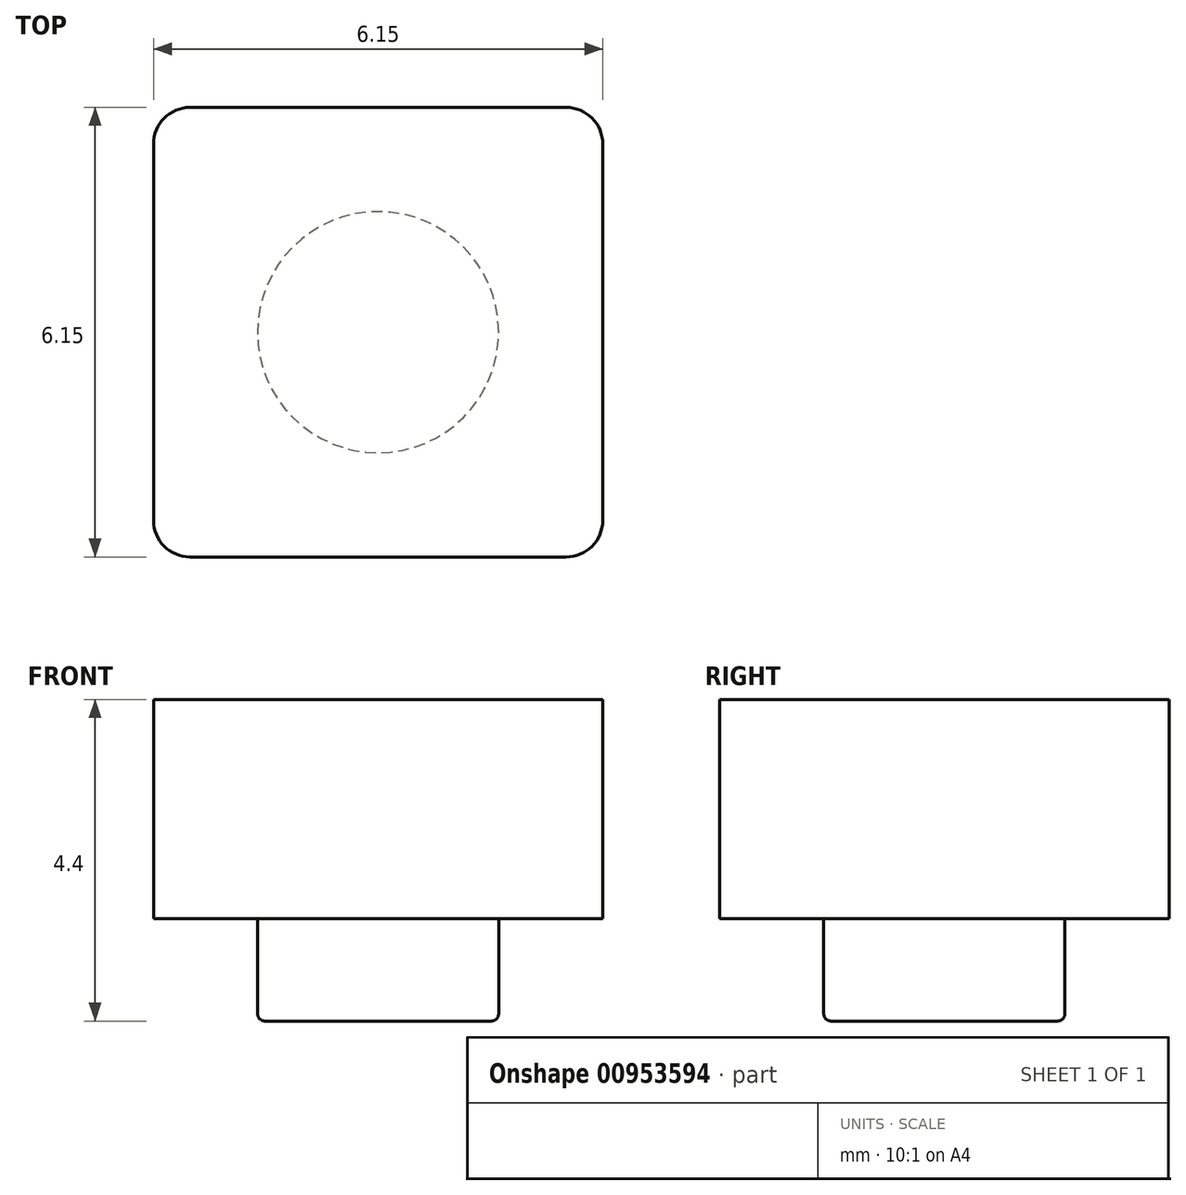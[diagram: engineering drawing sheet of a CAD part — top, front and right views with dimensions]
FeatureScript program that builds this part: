
annotation { "Feature Type Name" : "Feature", "Feature Type Description" : "" }
export const myFeature = defineFeature(function(context is Context, id is Id, definition is map)
    precondition{}
    {
        {
            var Q0;
            Q0=qCreatedBy(makeId("Top.planeOp"),FACE);
            var sketch = newSketch(context, id + "F0", { "sketchPlane" : qUnion([Q0])});
            skLineSegment(sketch, "E0.bottom", {"start": v(0, 0) * mm, "end": v(6.15, 0) * mm});
            skLineSegment(sketch, "E0.top", {"start": v(0, -6.15) * mm, "end": v(6.15, -6.15) * mm});
            skLineSegment(sketch, "E0.left", {"start": v(0, 0) * mm, "end": v(0, -6.15) * mm});
            skLineSegment(sketch, "E0.right", {"start": v(6.15, 0) * mm, "end": v(6.15, -6.15) * mm});
            skSolve(sketch);
        }
        {
            var Q0;
            Q0 = qSketchRegion(id + "F0", true);
            extrude(context, id + "F1", {"entities" : qUnion([Q0]), "depth" : 3 * mm, "offsetDistance" : 25 * mm});
        }
        {
            var Q0;
            Q0=makeQuery(id+"F1.opExtrude","SWEPT_EDGE",EDGE,{"disambiguationData":[OSD([sQuery(id+"F0.wireOp",EDGE,"E0.bottom"),sQuery(id+"F0.wireOp",EDGE,"E0.left")])]});
            var Q1;
            Q1=makeQuery(id+"F1.opExtrude","SWEPT_EDGE",EDGE,{"disambiguationData":[OSD([sQuery(id+"F0.wireOp",EDGE,"E0.bottom"),sQuery(id+"F0.wireOp",EDGE,"E0.right")])]});
            var Q2;
            Q2=makeQuery(id+"F1.opExtrude","SWEPT_EDGE",EDGE,{"disambiguationData":[OSD([sQuery(id+"F0.wireOp",EDGE,"E0.top"),sQuery(id+"F0.wireOp",EDGE,"E0.left")])]});
            var Q3;
            Q3=makeQuery(id+"F1.opExtrude","SWEPT_EDGE",EDGE,{"disambiguationData":[OSD([sQuery(id+"F0.wireOp",EDGE,"E0.top"),sQuery(id+"F0.wireOp",EDGE,"E0.right")])]});
            fillet(context, id + "F2", {"entities" : qUnion([Q0, Q1, Q2, Q3]), "radius" : 0.5 * mm, "tangentPropagation" : true, "allowEdgeOverflow" : false});
        }
        {
            var Q0;
            Q0=makeQuery(id+"F1.opExtrude","CAP_FACE",FACE,{"disambiguationData":[OSD([sQuery(id+"F0.wireOp",EDGE,"E0.bottom"),sQuery(id+"F0.wireOp",EDGE,"E0.top"),sQuery(id+"F0.wireOp",EDGE,"E0.left"),sQuery(id+"F0.wireOp",EDGE,"E0.right")])],"isStart":true});
            var sketch = newSketch(context, id + "F3", { "sketchPlane" : qUnion([Q0])});
            skCircle(sketch, "E1", {"center": v(3.07, 3.08) * mm, "radius": 1.65 * mm});
            skPoint(sketch, "E1.centerSnap0", {"position": v(0, 3.08) * mm});
            skPoint(sketch, "E1.centerSnap1", {"position": v(3.07, 6.15) * mm});
            skSolve(sketch);
        }
        {
            var Q0;
            Q0=makeQuery(id+"F3.imprint","IMPRINT",FACE,{"disambiguationData":[TD([[makeQuery(id+"F3.imprint","IMPRINT",EDGE,{"derivedFrom":sQuery(id+"F3.wireOp",EDGE,"E1")}),1.0]])]});
            extrude(context, id + "F4", {"entities" : qUnion([Q0]), "operationType" : NewBodyOperationType.ADD, "depth" : 1.4 * mm, "offsetDistance" : 25 * mm});
        }
        {
            var Q0;
            Q0=makeQuery(id+"F4.opExtrude","CAP_EDGE",EDGE,{"disambiguationData":[OSD([sQuery(id+"F3.wireOp",EDGE,"E1")])],"isStart":false});
            fillet(context, id + "F5", {"entities" : qUnion([Q0]), "radius" : 0.1 * mm, "tangentPropagation" : true, "allowEdgeOverflow" : false});
        }
    });
